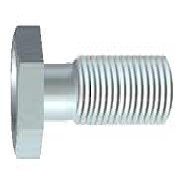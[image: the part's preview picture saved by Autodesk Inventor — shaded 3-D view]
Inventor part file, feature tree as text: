
AUTODESK INVENTOR PART (.ipt)
format: ipt  version: 2017 (Build 210142000, 142)  size: 178,688 bytes
history: native  units: mm (DEFAULTED — no unit token found)
features: sketch x4, extrude x2, chamfer x1, plane x1
ambient origin geometry x7: Origin, YZ Plane, XZ Plane, X Axis, Y Axis, Z Axis, Center Point
bodies: Solid1 (feature_tree), Body (feature_tree)
feature tree (8):
  extrude  "Head"  TaperAngle=90.0deg  [1 undecoded]
  extrude  "Indent"  TaperAngle=0.0deg  [1 undecoded]
  chamfer  "Chamfer1"  Distance=0.39751mm
  plane  "Work Plane1"
  sketch  "Sketch1"  dims[d1=4.1656mm d12=90.0deg]
  sketch  "Sketch2"  dims[d2=2.794mm d3=0.0mm]
  sketch  "Sketch4"  dims[d21=90.0deg d5=0.39751mm d6=0.39761mm d7=0.0mm d8=7.9248mm d9=26.9875mm d10=0.0mm d13=31.75mm d17=7.9248mm d18=6.33984mm d19=0.2804mm d20=0.0mm d77=45.0deg d80=0.0mm d81=0.0mm]
  sketch  "Sketch3"  dims[d4=30.0deg]
note: 2 required parameter values undecoded (feature->parameter linkage not recoverable at this tier; creation-order binding heuristic only, values carry confidence <= 0.55)
